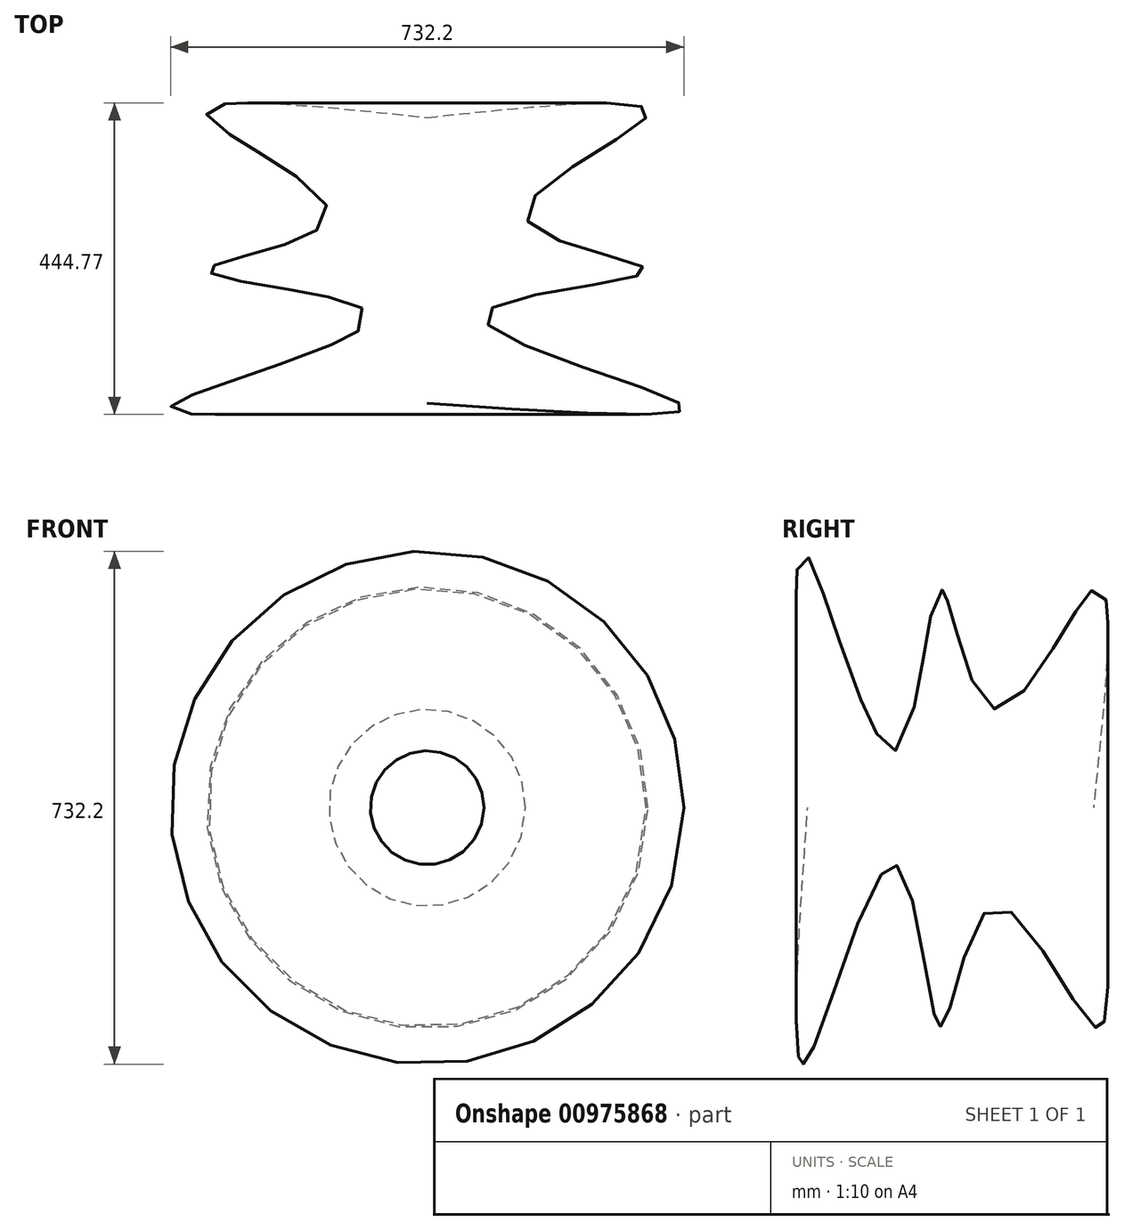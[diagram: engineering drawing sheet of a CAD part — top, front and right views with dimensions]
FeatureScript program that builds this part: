
annotation { "Feature Type Name" : "Feature", "Feature Type Description" : "" }
export const myFeature = defineFeature(function(context is Context, id is Id, definition is map)
    precondition{}
    {
        {
            var Q0;
            Q0=qCreatedBy(makeId("Top.planeOp"),FACE);
            var sketch = newSketch(context, id + "F0", { "sketchPlane" : qUnion([Q0])});
            skLineSegment(sketch, "E0", {"start": v(0, 407.67) * mm, "end": v(0, 0) * mm});
            skFitSpline(sketch, "E1", {"points": [v(0, 407.67) * mm, v(312.22, 407.67) * mm, v(141.2, 264.49) * mm, v(312.22, 188.92) * mm, v(81.53, 125.28) * mm, v(359.94, 0) * mm, v(0, 0) * mm], "startDerivative": vector(2825.4, 299.28) * mm, "endDerivative": vector(-3137.9, 220.06) * mm});
            skSolve(sketch);
        }
        {
            var Q0;
            Q0 = qSketchRegion(id + "F0", true);
            var Q1;
            Q1=sQuery(id+"F0.wireOp",EDGE,"E0");
            revolve(context, id + "F1", {"surfaceOperationType" : NewSurfaceOperationType.NEW, "entities" : qUnion([Q0]), "axis" : qUnion([Q1]), "revolveType" : RevolveType.FULL});
        }
    });
